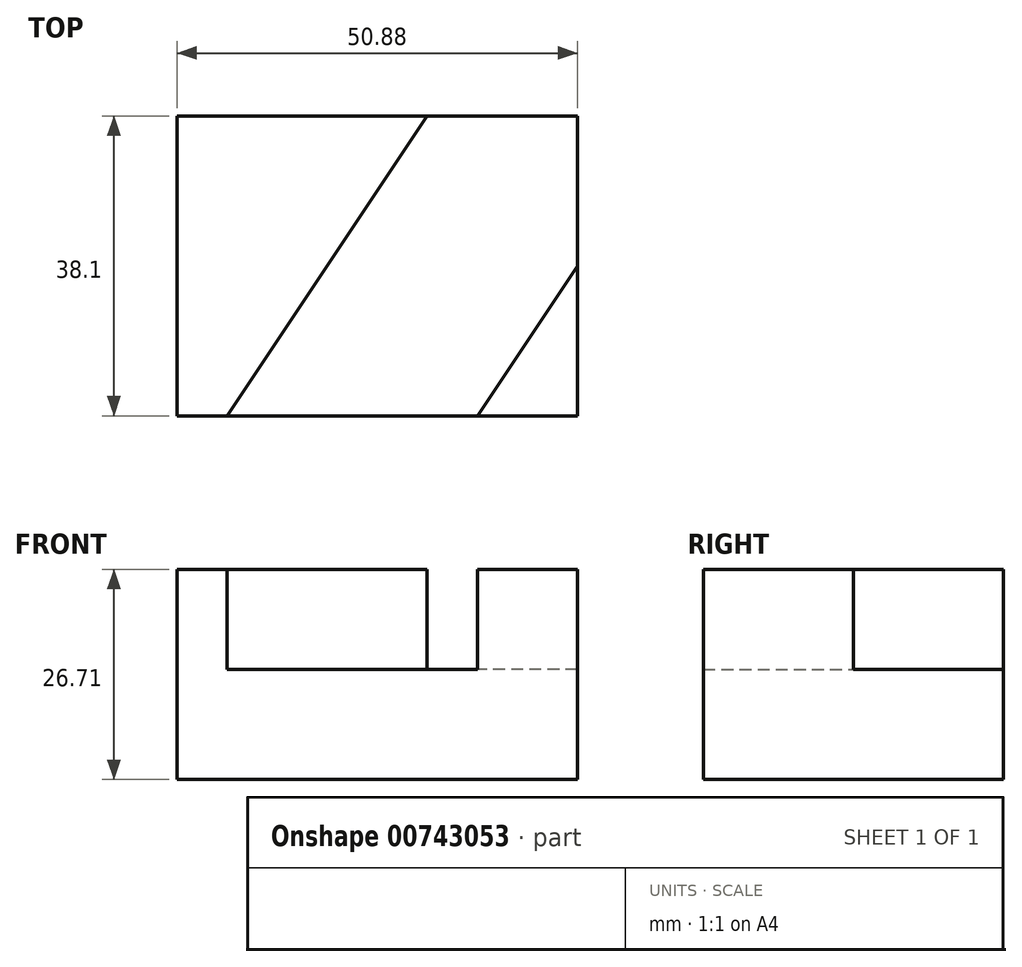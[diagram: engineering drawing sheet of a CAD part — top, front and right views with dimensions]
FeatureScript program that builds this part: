
annotation { "Feature Type Name" : "Feature", "Feature Type Description" : "" }
export const myFeature = defineFeature(function(context is Context, id is Id, definition is map)
    precondition{}
    {
        {
            var Q0;
            Q0=qCreatedBy(makeId("Front.planeOp"),FACE);
            var sketch = newSketch(context, id + "F0", { "sketchPlane" : qUnion([Q0])});
            skLineSegment(sketch, "E0", {"start": v(0, 0) * mm, "end": v(50.88, 0) * mm});
            skLineSegment(sketch, "E1", {"start": v(50.88, 0) * mm, "end": v(50.88, 26.71) * mm});
            skLineSegment(sketch, "E2", {"start": v(50.88, 26.71) * mm, "end": v(0, 26.71) * mm});
            skLineSegment(sketch, "E3", {"start": v(0, 26.71) * mm, "end": v(0, 0) * mm});
            skSolve(sketch);
        }
        {
            var Q0;
            Q0=makeQuery(id+"F0.imprint","IMPRINT",FACE,{"disambiguationData":[TD([[makeQuery(id+"F0.imprint","IMPRINT",EDGE,{"derivedFrom":sQuery(id+"F0.wireOp",EDGE,"E0")}),1.0]])]});
            extrude(context, id + "F1", {"entities" : qUnion([Q0]), "oppositeDirection" : true, "depth" : 38.1 * mm, "offsetDistance" : 25.4 * mm});
        }
        {
            var Q0;
            Q0=makeQuery(id+"F1.opExtrude","SWEPT_FACE",FACE,{"disambiguationData":[OSD([sQuery(id+"F0.wireOp",EDGE,"E2")])]});
            var sketch = newSketch(context, id + "F2", { "sketchPlane" : qUnion([Q0])});
            skLineSegment(sketch, "E4", {"start": v(6.35, 0) * mm, "end": v(31.75, 38.1) * mm});
            skLineSegment(sketch, "E5", {"start": v(50.88, 19.05) * mm, "end": v(38.18, 0) * mm});
            skSolve(sketch);
        }
        {
            var Q0;
            {var subQ0=sQuery(id+"F2.wireOp",EDGE,"E4");Q0=makeQuery(id+"F2.imprint","IMPRINT",FACE,{"disambiguationData":[TD([[makeQuery(id+"F2.imprint","IMPRINT",EDGE,{"derivedFrom":subQ0}),-1.0]])]});}
            extrude(context, id + "F3", {"entities" : qUnion([Q0]), "operationType" : NewBodyOperationType.REMOVE, "oppositeDirection" : true, "depth" : 12.7 * mm, "offsetDistance" : 25.4 * mm});
        }
    });
